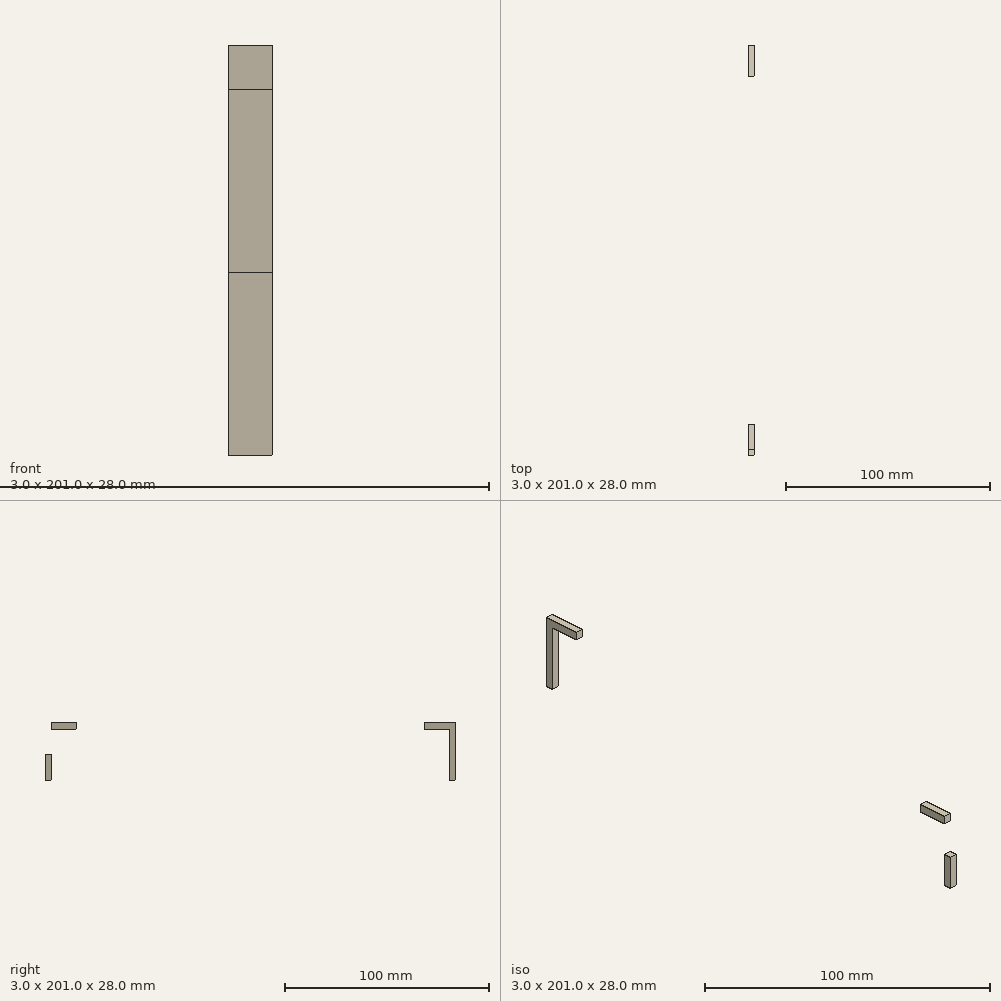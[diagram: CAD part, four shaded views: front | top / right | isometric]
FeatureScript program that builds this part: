
annotation { "Feature Type Name" : "Feature", "Feature Type Description" : "" }
export const myFeature = defineFeature(function(context is Context, id is Id, definition is map)
    precondition{}
    {
        {
            var Q0;
            Q0=qCreatedBy(makeId("Right.planeOp"),FACE);
            var sketch = newSketch(context, id + "F0", { "sketchPlane" : qUnion([Q0])});
            skLineSegment(sketch, "E0.bottom", {"start": v(0, 0) * mm, "end": v(201, 0) * mm});
            skLineSegment(sketch, "E0.top", {"start": v(0, 25) * mm, "end": v(201, 25) * mm});
            skLineSegment(sketch, "E0.left", {"start": v(0, 0) * mm, "end": v(0, 25) * mm});
            skLineSegment(sketch, "E0.right", {"start": v(201, 0) * mm, "end": v(201, 25) * mm});
            skPoint(sketch, "E1.oppositeSnap0", {"position": v(0, 12.5) * mm});
            skLineSegment(sketch, "E1.bottom", {"start": v(0, 0) * mm, "end": v(3, 0) * mm});
            skLineSegment(sketch, "E1.top", {"start": v(0, 12.5) * mm, "end": v(3, 12.5) * mm});
            skLineSegment(sketch, "E1.left", {"start": v(0, 0) * mm, "end": v(0, 12.5) * mm});
            skLineSegment(sketch, "E1.right", {"start": v(3, 0) * mm, "end": v(3, 12.5) * mm});
            skLineSegment(sketch, "E2", {"start": v(3, 12.5) * mm, "end": v(3, 25) * mm});
            skPoint(sketch, "E3.oppositeSnap0", {"position": v(201, 12.5) * mm});
            skLineSegment(sketch, "E3.bottom", {"start": v(201, 0) * mm, "end": v(198, 0) * mm});
            skLineSegment(sketch, "E3.top", {"start": v(201, 12.5) * mm, "end": v(198, 12.5) * mm});
            skLineSegment(sketch, "E3.left", {"start": v(201, 0) * mm, "end": v(201, 12.5) * mm});
            skLineSegment(sketch, "E3.right", {"start": v(198, 0) * mm, "end": v(198, 12.5) * mm});
            skLineSegment(sketch, "E4", {"start": v(198, 12.5) * mm, "end": v(198, 25) * mm});
            skLineSegment(sketch, "E5.bottom", {"start": v(201, 25) * mm, "end": v(186, 25) * mm});
            skLineSegment(sketch, "E5.top", {"start": v(201, 28) * mm, "end": v(186, 28) * mm});
            skLineSegment(sketch, "E5.left", {"start": v(201, 25) * mm, "end": v(201, 28) * mm});
            skLineSegment(sketch, "E5.right", {"start": v(186, 25) * mm, "end": v(186, 28) * mm});
            skLineSegment(sketch, "E6.bottom", {"start": v(0, 25) * mm, "end": v(15, 25) * mm});
            skLineSegment(sketch, "E6.top", {"start": v(0, 28) * mm, "end": v(15, 28) * mm});
            skLineSegment(sketch, "E6.left", {"start": v(0, 25) * mm, "end": v(0, 28) * mm});
            skLineSegment(sketch, "E6.right", {"start": v(15, 25) * mm, "end": v(15, 28) * mm});
            skLineSegment(sketch, "E7", {"start": v(3, 25) * mm, "end": v(3, 28) * mm});
            skSolve(sketch);
        }
        {
            var Q0;
            {var subQ0=sQuery(id+"F0.wireOp",EDGE,"E6.right");Q0=makeQuery(id+"F0.imprint","IMPRINT",FACE,{"disambiguationData":[TD([[makeQuery(id+"F0.imprint","IMPRINT",EDGE,{"derivedFrom":subQ0}),1.0]])]});}
            var Q1;
            Q1=makeQuery(id+"F0.imprint","IMPRINT",FACE,{"disambiguationData":[TD([[makeQuery(id+"F0.imprint","IMPRINT",EDGE,{"derivedFrom":sQuery(id+"F0.wireOp",EDGE,"E1.bottom")}),1.0]])]});
            var Q2;
            Q2=makeQuery(id+"F0.imprint","IMPRINT",FACE,{"disambiguationData":[TD([[makeQuery(id+"F0.imprint","IMPRINT",EDGE,{"derivedFrom":sQuery(id+"F0.wireOp",EDGE,"E0.bottom")}),1.0]])]});
            var Q3;
            {var subQ0=sQuery(id+"F0.wireOp",EDGE,"E0.right");Q3=makeQuery(id+"F0.imprint","IMPRINT",FACE,{"disambiguationData":[TD([[makeQuery(id+"F0.imprint","IMPRINT",EDGE,{"derivedFrom":subQ0}),1.0]])]});}
            var Q4;
            Q4=makeQuery(id+"F0.imprint","IMPRINT",FACE,{"disambiguationData":[TD([[makeQuery(id+"F0.imprint","IMPRINT",EDGE,{"derivedFrom":sQuery(id+"F0.wireOp",EDGE,"E5.top")}),1.0]])]});
            extrude(context, id + "F1", {"entities" : qUnion([Q0, Q1, Q2, Q3, Q4]), "depth" : 3 * mm, "offsetDistance" : 25 * mm});
        }
    });
